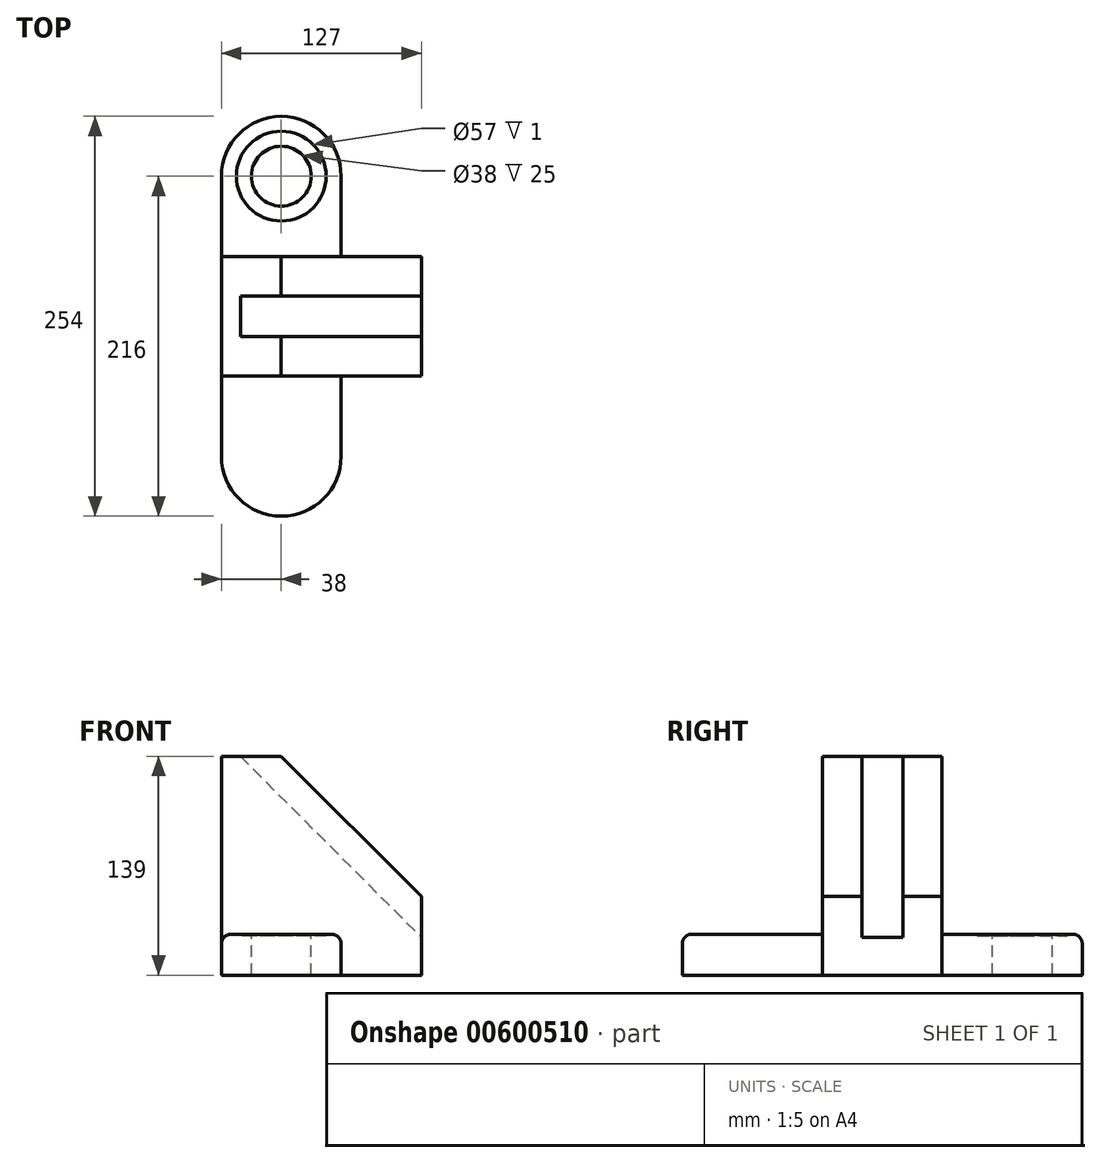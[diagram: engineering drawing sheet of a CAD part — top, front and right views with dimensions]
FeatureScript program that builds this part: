
annotation { "Feature Type Name" : "Feature", "Feature Type Description" : "" }
export const myFeature = defineFeature(function(context is Context, id is Id, definition is map)
    precondition{}
    {
        {
            var Q0;
            Q0=qCreatedBy(makeId("Top.planeOp"),FACE);
            var sketch = newSketch(context, id + "F0", { "sketchPlane" : qUnion([Q0])});
            skLineSegment(sketch, "E0.left", {"start": v(38, 89) * mm, "end": v(38, -89) * mm});
            skLineSegment(sketch, "E0.right", {"start": v(-38, 89) * mm, "end": v(-38, -89) * mm});
            skPoint(sketch, "E0.middle", {"position": v(0, 0) * mm});
            skArc(sketch, "E1", {"start": v(38, 89) * mm, "mid": v(0, 127) * mm, "end": v(-38, 89) * mm});
            skArc(sketch, "E2", {"start": v(-38, -89) * mm, "mid": v(0, -127) * mm, "end": v(38, -89) * mm});
            skSolve(sketch);
        }
        {
            var Q0;
            Q0 = qSketchRegion(id + "F0", true);
            extrude(context, id + "F1", {"entities" : qUnion([Q0]), "depth" : 26 * mm, "offsetDistance" : 25 * mm});
        }
        {
            var Q0;
            Q0=makeQuery(id+"F1.opExtrude","CAP_FACE",FACE,{"disambiguationData":[OSD([sQuery(id+"F0.wireOp",EDGE,"E0.left"),sQuery(id+"F0.wireOp",EDGE,"E0.right"),sQuery(id+"F0.wireOp",EDGE,"E1"),sQuery(id+"F0.wireOp",EDGE,"E2")])],"isStart":true});
            var sketch = newSketch(context, id + "F2", { "sketchPlane" : qUnion([Q0])});
            skLineSegment(sketch, "E3.bottom", {"start": v(-38, 38) * mm, "end": v(89, 38) * mm});
            skLineSegment(sketch, "E3.top", {"start": v(-38, -38) * mm, "end": v(89, -38) * mm});
            skLineSegment(sketch, "E3.left", {"start": v(-38, 38) * mm, "end": v(-38, -38) * mm});
            skLineSegment(sketch, "E3.right", {"start": v(89, 38) * mm, "end": v(89, -38) * mm});
            skSolve(sketch);
        }
        {
            var Q0;
            Q0=qCreatedBy(makeId("Front.planeOp"),FACE);
            cPlane(context, id + "F3", {"entities" : qUnion([Q0]), "cplaneType" : CPlaneType.OFFSET, "offset" : 38 * mm, "width" : 150 * mm, "height" : 150 * mm});
        }
        {
            var Q0;
            Q0=qCreatedBy(id+"F3.planeOp",FACE);
            var sketch = newSketch(context, id + "F4", { "sketchPlane" : qUnion([Q0])});
            skLineSegment(sketch, "E4.bottom", {"start": v(-38, 0) * mm, "end": v(89, 0) * mm});
            skLineSegment(sketch, "E4.left", {"start": v(-38, 0) * mm, "end": v(-38, 50) * mm});
            skLineSegment(sketch, "E4.right", {"start": v(89, 0) * mm, "end": v(89, 50) * mm});
            skLineSegment(sketch, "E5", {"start": v(89, 50) * mm, "end": v(0, 139) * mm});
            skLineSegment(sketch, "E6.top", {"start": v(-38, 139) * mm, "end": v(0, 139) * mm});
            skLineSegment(sketch, "E6.left", {"start": v(-38, 50) * mm, "end": v(-38, 139) * mm});
            skSolve(sketch);
        }
        {
            var Q0;
            Q0 = qSketchRegion(id + "F4", true);
            extrude(context, id + "F5", {"entities" : qUnion([Q0]), "operationType" : NewBodyOperationType.ADD, "oppositeDirection" : true, "depth" : 76 * mm, "offsetDistance" : 25 * mm});
        }
        {
            var Q0;
            Q0=qCreatedBy(makeId("Front.planeOp"),FACE);
            cPlane(context, id + "F6", {"entities" : qUnion([Q0]), "cplaneType" : CPlaneType.OFFSET, "offset" : 13 * mm, "width" : 150 * mm, "height" : 150 * mm});
        }
        {
            var Q0;
            Q0=qCreatedBy(id+"F6.planeOp",FACE);
            var sketch = newSketch(context, id + "F7", { "sketchPlane" : qUnion([Q0])});
            skLineSegment(sketch, "E7", {"start": v(0, 139) * mm, "end": v(-26, 139) * mm});
            skLineSegment(sketch, "E8", {"start": v(-26, 139) * mm, "end": v(89, 24) * mm});
            skLineSegment(sketch, "E9", {"start": v(89, 24) * mm, "end": v(89, 50) * mm});
            skLineSegment(sketch, "E10", {"start": v(89, 50) * mm, "end": v(0, 139) * mm});
            skSolve(sketch);
        }
        {
            var Q0;
            Q0 = qSketchRegion(id + "F7", true);
            extrude(context, id + "F8", {"entities" : qUnion([Q0]), "operationType" : NewBodyOperationType.REMOVE, "oppositeDirection" : true, "depth" : 26 * mm, "offsetDistance" : 25 * mm});
        }
        {
            var Q0;
            {var subQ0=sQuery(id+"F0.wireOp",EDGE,"E1");var subQ3=sQuery(id+"F0.wireOp",EDGE,"E0.right");var subQ4=sQuery(id+"F0.wireOp",EDGE,"E0.left");Q0=makeQuery(id+"F5.boolean.opBoolean","SPLIT",FACE,{"disambiguationData":[TD([makeQuery(id+"F1.opExtrude","SWEPT_FACE",FACE,{"disambiguationData":[OSD([subQ0])]})])],"derivedFrom":makeQuery(id+"F1.opExtrude","CAP_FACE",FACE,{"disambiguationData":[OSD([subQ4,subQ3,subQ0,sQuery(id+"F0.wireOp",EDGE,"E2")])],"isStart":false})});}
            var sketch = newSketch(context, id + "F9", { "sketchPlane" : qUnion([Q0])});
            skCircle(sketch, "E11", {"center": v(0, 89) * mm, "radius": 28.5 * mm});
            skSolve(sketch);
        }
        {
            var Q0;
            Q0 = qSketchRegion(id + "F9", true);
            extrude(context, id + "F10", {"entities" : qUnion([Q0]), "operationType" : NewBodyOperationType.REMOVE, "oppositeDirection" : true, "depth" : 1 * mm, "offsetDistance" : 25 * mm});
        }
        {
            var Q0;
            Q0=makeQuery(id+"F10.boolean.opBoolean","COPY",FACE,{"derivedFrom":makeQuery(id+"F10.opExtrude","CAP_FACE",FACE,{"disambiguationData":[OSD([sQuery(id+"F9.wireOp",EDGE,"E11")])],"isStart":false})});
            var sketch = newSketch(context, id + "F11", { "sketchPlane" : qUnion([Q0])});
            skCircle(sketch, "E12", {"center": v(0, 89) * mm, "radius": 19 * mm});
            skSolve(sketch);
        }
        {
            var Q0;
            Q0 = qSketchRegion(id + "F11", true);
            extrude(context, id + "F12", {"entities" : qUnion([Q0]), "operationType" : NewBodyOperationType.REMOVE, "endBound" : BoundingType.UP_TO_NEXT, "oppositeDirection" : true, "depth" : 25 * mm, "offsetDistance" : 25 * mm});
        }
        {
            var Q0;
            {var subQ0=sQuery(id+"F0.wireOp",EDGE,"E0.left");var subQ1=sQuery(id+"F0.wireOp",EDGE,"E2");Q0=makeQuery(id+"F5.boolean.opBoolean","SPLIT",EDGE,{"disambiguationData":[TD([makeQuery(id+"F1.opExtrude","SWEPT_FACE",FACE,{"disambiguationData":[OSD([subQ1])]})])],"derivedFrom":makeQuery(id+"F1.opExtrude","CAP_EDGE",EDGE,{"disambiguationData":[OSD([subQ0])],"isStart":false})});}
            var Q1;
            {var subQ0=sQuery(id+"F0.wireOp",EDGE,"E0.left");var subQ1=sQuery(id+"F0.wireOp",EDGE,"E1");Q1=makeQuery(id+"F5.boolean.opBoolean","SPLIT",EDGE,{"disambiguationData":[TD([makeQuery(id+"F1.opExtrude","SWEPT_FACE",FACE,{"disambiguationData":[OSD([subQ1])]})])],"derivedFrom":makeQuery(id+"F1.opExtrude","CAP_EDGE",EDGE,{"disambiguationData":[OSD([subQ0])],"isStart":false})});}
            fillet(context, id + "F13", {"entities" : qUnion([Q0, Q1]), "radius" : 6 * mm, "tangentPropagation" : true, "allowEdgeOverflow" : false});
        }
    });
